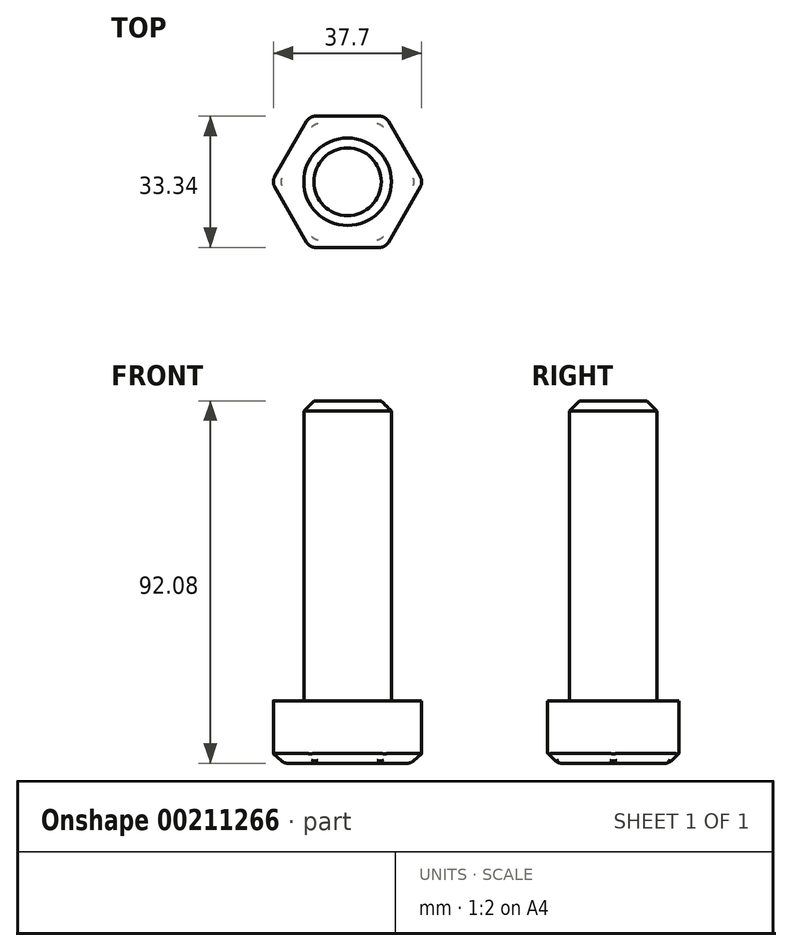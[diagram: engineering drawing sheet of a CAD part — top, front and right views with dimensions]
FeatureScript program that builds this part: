
annotation { "Feature Type Name" : "Feature", "Feature Type Description" : "" }
export const myFeature = defineFeature(function(context is Context, id is Id, definition is map)
    precondition{}
    {
        {
            var Q0;
            Q0=qCreatedBy(makeId("Top.planeOp"),FACE);
            var sketch = newSketch(context, id + "F0", { "sketchPlane" : qUnion([Q0])});
            skCircle(sketch, "E0.cCircle", {"center": v(0, 0) * mm, "radius": 16.67 * mm, "construction": true});
            skLineSegment(sketch, "E0.0", {"start": v(-9.62, 16.67) * mm, "end": v(9.62, 16.67) * mm});
            skLineSegment(sketch, "E0.1", {"start": v(9.62, 16.67) * mm, "end": v(19.25, 0) * mm});
            skLineSegment(sketch, "E0.2", {"start": v(19.25, 0) * mm, "end": v(9.62, -16.67) * mm});
            skLineSegment(sketch, "E0.3", {"start": v(9.62, -16.67) * mm, "end": v(-9.62, -16.67) * mm});
            skLineSegment(sketch, "E0.4", {"start": v(-9.62, -16.67) * mm, "end": v(-19.25, 0) * mm});
            skLineSegment(sketch, "E0.5", {"start": v(-19.25, 0) * mm, "end": v(-9.62, 16.67) * mm});
            skPoint(sketch, "E0.0.midPoint", {"position": v(0, 16.67) * mm});
            skSolve(sketch);
        }
        {
            var Q0;
            Q0 = qSketchRegion(id + "F0", true);
            extrude(context, id + "F1", {"entities" : qUnion([Q0]), "depth" : 15.88 * mm});
        }
        {
            var Q0;
            Q0=makeQuery(id+"F1.opExtrude","CAP_FACE",FACE,{"disambiguationData":[OSD([sQuery(id+"F0.wireOp",EDGE,"E0.0"),sQuery(id+"F0.wireOp",EDGE,"E0.1"),sQuery(id+"F0.wireOp",EDGE,"E0.2"),sQuery(id+"F0.wireOp",EDGE,"E0.3"),sQuery(id+"F0.wireOp",EDGE,"E0.4"),sQuery(id+"F0.wireOp",EDGE,"E0.5")])],"isStart":false});
            var sketch = newSketch(context, id + "F2", { "sketchPlane" : qUnion([Q0])});
            skCircle(sketch, "E1", {"center": v(0, 0) * mm, "radius": 11.11 * mm});
            skSolve(sketch);
        }
        {
            var Q0;
            Q0 = qSketchRegion(id + "F2", true);
            extrude(context, id + "F3", {"entities" : qUnion([Q0]), "operationType" : NewBodyOperationType.ADD, "depth" : 76.2 * mm});
        }
        {
            var Q0;
            Q0=makeQuery(id+"F3.opExtrude","CAP_EDGE",EDGE,{"disambiguationData":[OSD([sQuery(id+"F2.wireOp",EDGE,"E1")])],"isStart":false});
            var Q1;
            Q1=makeQuery(id+"F1.opExtrude","CAP_EDGE",EDGE,{"disambiguationData":[OSD([sQuery(id+"F0.wireOp",EDGE,"E0.5")])],"isStart":true});
            var Q2;
            Q2=makeQuery(id+"F1.opExtrude","CAP_EDGE",EDGE,{"disambiguationData":[OSD([sQuery(id+"F0.wireOp",EDGE,"E0.0")])],"isStart":true});
            var Q3;
            Q3=makeQuery(id+"F1.opExtrude","CAP_EDGE",EDGE,{"disambiguationData":[OSD([sQuery(id+"F0.wireOp",EDGE,"E0.1")])],"isStart":true});
            var Q4;
            Q4=makeQuery(id+"F1.opExtrude","CAP_EDGE",EDGE,{"disambiguationData":[OSD([sQuery(id+"F0.wireOp",EDGE,"E0.2")])],"isStart":true});
            var Q5;
            Q5=makeQuery(id+"F1.opExtrude","CAP_EDGE",EDGE,{"disambiguationData":[OSD([sQuery(id+"F0.wireOp",EDGE,"E0.3")])],"isStart":true});
            var Q6;
            Q6=makeQuery(id+"F1.opExtrude","CAP_EDGE",EDGE,{"disambiguationData":[OSD([sQuery(id+"F0.wireOp",EDGE,"E0.4")])],"isStart":true});
            chamfer(context, id + "F4", {"entities" : qUnion([Q0, Q1, Q2, Q3, Q4, Q5, Q6]), "width" : 2.54 * mm, "tangentPropagation" : true});
        }
        {
            var Q0;
            Q0=makeQuery(id+"F1.opExtrude","SWEPT_EDGE",EDGE,{"disambiguationData":[OSD([sQuery(id+"F0.wireOp",EDGE,"E0.0"),sQuery(id+"F0.wireOp",EDGE,"E0.5")])]});
            var Q1;
            Q1=makeQuery(id+"F1.opExtrude","SWEPT_EDGE",EDGE,{"disambiguationData":[OSD([sQuery(id+"F0.wireOp",EDGE,"E0.0"),sQuery(id+"F0.wireOp",EDGE,"E0.1")])]});
            var Q2;
            Q2=makeQuery(id+"F1.opExtrude","SWEPT_EDGE",EDGE,{"disambiguationData":[OSD([sQuery(id+"F0.wireOp",EDGE,"E0.1"),sQuery(id+"F0.wireOp",EDGE,"E0.2")])]});
            var Q3;
            Q3=makeQuery(id+"F1.opExtrude","SWEPT_EDGE",EDGE,{"disambiguationData":[OSD([sQuery(id+"F0.wireOp",EDGE,"E0.2"),sQuery(id+"F0.wireOp",EDGE,"E0.3")])]});
            var Q4;
            Q4=makeQuery(id+"F1.opExtrude","SWEPT_EDGE",EDGE,{"disambiguationData":[OSD([sQuery(id+"F0.wireOp",EDGE,"E0.3"),sQuery(id+"F0.wireOp",EDGE,"E0.4")])]});
            var Q5;
            Q5=makeQuery(id+"F1.opExtrude","SWEPT_EDGE",EDGE,{"disambiguationData":[OSD([sQuery(id+"F0.wireOp",EDGE,"E0.4"),sQuery(id+"F0.wireOp",EDGE,"E0.5")])]});
            var Q6;
            Q6=makeQuery(id+"F4.opChamfer","BLEND_EDGE",EDGE,{"blendedFrom":[makeQuery(id+"F1.opExtrude","CAP_EDGE",EDGE,{"disambiguationData":[OSD([sQuery(id+"F0.wireOp",EDGE,"E0.3")])],"isStart":true}),makeQuery(id+"F1.opExtrude","CAP_EDGE",EDGE,{"disambiguationData":[OSD([sQuery(id+"F0.wireOp",EDGE,"E0.4")])],"isStart":true})],"blendedInto":[]});
            var Q7;
            Q7=makeQuery(id+"F4.opChamfer","BLEND_EDGE",EDGE,{"blendedFrom":[makeQuery(id+"F1.opExtrude","CAP_EDGE",EDGE,{"disambiguationData":[OSD([sQuery(id+"F0.wireOp",EDGE,"E0.2")])],"isStart":true}),makeQuery(id+"F1.opExtrude","CAP_EDGE",EDGE,{"disambiguationData":[OSD([sQuery(id+"F0.wireOp",EDGE,"E0.3")])],"isStart":true})],"blendedInto":[]});
            var Q8;
            Q8=makeQuery(id+"F4.opChamfer","BLEND_EDGE",EDGE,{"blendedFrom":[makeQuery(id+"F1.opExtrude","CAP_EDGE",EDGE,{"disambiguationData":[OSD([sQuery(id+"F0.wireOp",EDGE,"E0.1")])],"isStart":true}),makeQuery(id+"F1.opExtrude","CAP_EDGE",EDGE,{"disambiguationData":[OSD([sQuery(id+"F0.wireOp",EDGE,"E0.2")])],"isStart":true})],"blendedInto":[]});
            var Q9;
            Q9=makeQuery(id+"F4.opChamfer","BLEND_EDGE",EDGE,{"blendedFrom":[makeQuery(id+"F1.opExtrude","CAP_EDGE",EDGE,{"disambiguationData":[OSD([sQuery(id+"F0.wireOp",EDGE,"E0.0")])],"isStart":true}),makeQuery(id+"F1.opExtrude","CAP_EDGE",EDGE,{"disambiguationData":[OSD([sQuery(id+"F0.wireOp",EDGE,"E0.1")])],"isStart":true})],"blendedInto":[]});
            var Q10;
            Q10=makeQuery(id+"F4.opChamfer","BLEND_EDGE",EDGE,{"blendedFrom":[makeQuery(id+"F1.opExtrude","CAP_EDGE",EDGE,{"disambiguationData":[OSD([sQuery(id+"F0.wireOp",EDGE,"E0.0")])],"isStart":true}),makeQuery(id+"F1.opExtrude","CAP_EDGE",EDGE,{"disambiguationData":[OSD([sQuery(id+"F0.wireOp",EDGE,"E0.5")])],"isStart":true})],"blendedInto":[]});
            var Q11;
            Q11=makeQuery(id+"F4.opChamfer","BLEND_EDGE",EDGE,{"blendedFrom":[makeQuery(id+"F1.opExtrude","CAP_EDGE",EDGE,{"disambiguationData":[OSD([sQuery(id+"F0.wireOp",EDGE,"E0.4")])],"isStart":true}),makeQuery(id+"F1.opExtrude","CAP_EDGE",EDGE,{"disambiguationData":[OSD([sQuery(id+"F0.wireOp",EDGE,"E0.5")])],"isStart":true})],"blendedInto":[]});
            var Q12;
            {var subQ0=sQuery(id+"F0.wireOp",EDGE,"E0.4");Q12=makeQuery(id+"F4.opChamfer","BLEND_EDGE",EDGE,{"blendedFrom":[makeQuery(id+"F1.opExtrude","CAP_EDGE",EDGE,{"disambiguationData":[OSD([subQ0])],"isStart":true}),makeQuery(id+"F1.opExtrude","CAP_FACE",FACE,{"disambiguationData":[OSD([sQuery(id+"F0.wireOp",EDGE,"E0.0"),sQuery(id+"F0.wireOp",EDGE,"E0.1"),sQuery(id+"F0.wireOp",EDGE,"E0.2"),sQuery(id+"F0.wireOp",EDGE,"E0.3"),subQ0,sQuery(id+"F0.wireOp",EDGE,"E0.5")])],"isStart":true})],"blendedInto":[makeQuery(id+"F1.opExtrude","CAP_FACE",FACE,{"disambiguationData":[OSD([sQuery(id+"F0.wireOp",EDGE,"E0.0"),sQuery(id+"F0.wireOp",EDGE,"E0.1"),sQuery(id+"F0.wireOp",EDGE,"E0.2"),sQuery(id+"F0.wireOp",EDGE,"E0.3"),subQ0,sQuery(id+"F0.wireOp",EDGE,"E0.5")])],"isStart":true})]});}
            var Q13;
            {var subQ0=sQuery(id+"F0.wireOp",EDGE,"E0.3");Q13=makeQuery(id+"F4.opChamfer","BLEND_EDGE",EDGE,{"blendedFrom":[makeQuery(id+"F1.opExtrude","CAP_EDGE",EDGE,{"disambiguationData":[OSD([subQ0])],"isStart":true}),makeQuery(id+"F1.opExtrude","CAP_FACE",FACE,{"disambiguationData":[OSD([sQuery(id+"F0.wireOp",EDGE,"E0.0"),sQuery(id+"F0.wireOp",EDGE,"E0.1"),sQuery(id+"F0.wireOp",EDGE,"E0.2"),subQ0,sQuery(id+"F0.wireOp",EDGE,"E0.4"),sQuery(id+"F0.wireOp",EDGE,"E0.5")])],"isStart":true})],"blendedInto":[makeQuery(id+"F1.opExtrude","CAP_FACE",FACE,{"disambiguationData":[OSD([sQuery(id+"F0.wireOp",EDGE,"E0.0"),sQuery(id+"F0.wireOp",EDGE,"E0.1"),sQuery(id+"F0.wireOp",EDGE,"E0.2"),subQ0,sQuery(id+"F0.wireOp",EDGE,"E0.4"),sQuery(id+"F0.wireOp",EDGE,"E0.5")])],"isStart":true})]});}
            var Q14;
            {var subQ0=sQuery(id+"F0.wireOp",EDGE,"E0.2");Q14=makeQuery(id+"F4.opChamfer","BLEND_EDGE",EDGE,{"blendedFrom":[makeQuery(id+"F1.opExtrude","CAP_EDGE",EDGE,{"disambiguationData":[OSD([subQ0])],"isStart":true}),makeQuery(id+"F1.opExtrude","CAP_FACE",FACE,{"disambiguationData":[OSD([sQuery(id+"F0.wireOp",EDGE,"E0.0"),sQuery(id+"F0.wireOp",EDGE,"E0.1"),subQ0,sQuery(id+"F0.wireOp",EDGE,"E0.3"),sQuery(id+"F0.wireOp",EDGE,"E0.4"),sQuery(id+"F0.wireOp",EDGE,"E0.5")])],"isStart":true})],"blendedInto":[makeQuery(id+"F1.opExtrude","CAP_FACE",FACE,{"disambiguationData":[OSD([sQuery(id+"F0.wireOp",EDGE,"E0.0"),sQuery(id+"F0.wireOp",EDGE,"E0.1"),subQ0,sQuery(id+"F0.wireOp",EDGE,"E0.3"),sQuery(id+"F0.wireOp",EDGE,"E0.4"),sQuery(id+"F0.wireOp",EDGE,"E0.5")])],"isStart":true})]});}
            var Q15;
            {var subQ0=sQuery(id+"F0.wireOp",EDGE,"E0.1");Q15=makeQuery(id+"F4.opChamfer","BLEND_EDGE",EDGE,{"blendedFrom":[makeQuery(id+"F1.opExtrude","CAP_EDGE",EDGE,{"disambiguationData":[OSD([subQ0])],"isStart":true}),makeQuery(id+"F1.opExtrude","CAP_FACE",FACE,{"disambiguationData":[OSD([sQuery(id+"F0.wireOp",EDGE,"E0.0"),subQ0,sQuery(id+"F0.wireOp",EDGE,"E0.2"),sQuery(id+"F0.wireOp",EDGE,"E0.3"),sQuery(id+"F0.wireOp",EDGE,"E0.4"),sQuery(id+"F0.wireOp",EDGE,"E0.5")])],"isStart":true})],"blendedInto":[makeQuery(id+"F1.opExtrude","CAP_FACE",FACE,{"disambiguationData":[OSD([sQuery(id+"F0.wireOp",EDGE,"E0.0"),subQ0,sQuery(id+"F0.wireOp",EDGE,"E0.2"),sQuery(id+"F0.wireOp",EDGE,"E0.3"),sQuery(id+"F0.wireOp",EDGE,"E0.4"),sQuery(id+"F0.wireOp",EDGE,"E0.5")])],"isStart":true})]});}
            var Q16;
            {var subQ0=sQuery(id+"F0.wireOp",EDGE,"E0.0");Q16=makeQuery(id+"F4.opChamfer","BLEND_EDGE",EDGE,{"blendedFrom":[makeQuery(id+"F1.opExtrude","CAP_EDGE",EDGE,{"disambiguationData":[OSD([subQ0])],"isStart":true}),makeQuery(id+"F1.opExtrude","CAP_FACE",FACE,{"disambiguationData":[OSD([subQ0,sQuery(id+"F0.wireOp",EDGE,"E0.1"),sQuery(id+"F0.wireOp",EDGE,"E0.2"),sQuery(id+"F0.wireOp",EDGE,"E0.3"),sQuery(id+"F0.wireOp",EDGE,"E0.4"),sQuery(id+"F0.wireOp",EDGE,"E0.5")])],"isStart":true})],"blendedInto":[makeQuery(id+"F1.opExtrude","CAP_FACE",FACE,{"disambiguationData":[OSD([subQ0,sQuery(id+"F0.wireOp",EDGE,"E0.1"),sQuery(id+"F0.wireOp",EDGE,"E0.2"),sQuery(id+"F0.wireOp",EDGE,"E0.3"),sQuery(id+"F0.wireOp",EDGE,"E0.4"),sQuery(id+"F0.wireOp",EDGE,"E0.5")])],"isStart":true})]});}
            var Q17;
            {var subQ0=sQuery(id+"F0.wireOp",EDGE,"E0.5");Q17=makeQuery(id+"F4.opChamfer","BLEND_EDGE",EDGE,{"blendedFrom":[makeQuery(id+"F1.opExtrude","CAP_EDGE",EDGE,{"disambiguationData":[OSD([subQ0])],"isStart":true}),makeQuery(id+"F1.opExtrude","CAP_FACE",FACE,{"disambiguationData":[OSD([sQuery(id+"F0.wireOp",EDGE,"E0.0"),sQuery(id+"F0.wireOp",EDGE,"E0.1"),sQuery(id+"F0.wireOp",EDGE,"E0.2"),sQuery(id+"F0.wireOp",EDGE,"E0.3"),sQuery(id+"F0.wireOp",EDGE,"E0.4"),subQ0])],"isStart":true})],"blendedInto":[makeQuery(id+"F1.opExtrude","CAP_FACE",FACE,{"disambiguationData":[OSD([sQuery(id+"F0.wireOp",EDGE,"E0.0"),sQuery(id+"F0.wireOp",EDGE,"E0.1"),sQuery(id+"F0.wireOp",EDGE,"E0.2"),sQuery(id+"F0.wireOp",EDGE,"E0.3"),sQuery(id+"F0.wireOp",EDGE,"E0.4"),subQ0])],"isStart":true})]});}
            fillet(context, id + "F5", {"entities" : qUnion([Q0, Q1, Q2, Q3, Q4, Q5, Q6, Q7, Q8, Q9, Q10, Q11, Q12, Q13, Q14, Q15, Q16, Q17]), "radius" : 2.54 * mm, "tangentPropagation" : true, "allowEdgeOverflow" : false});
        }
    });
